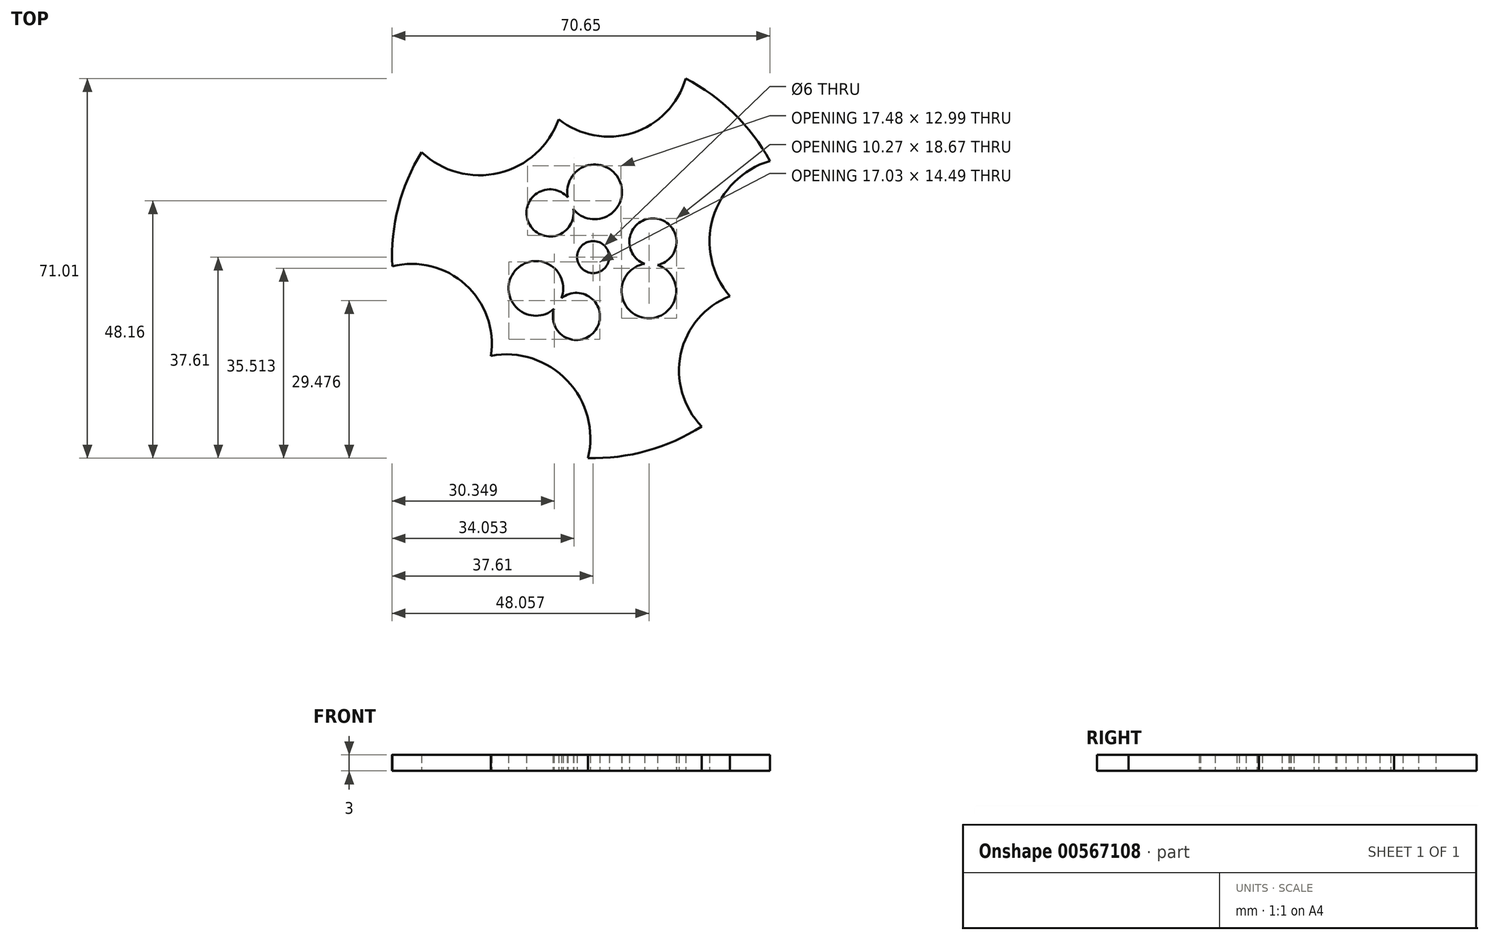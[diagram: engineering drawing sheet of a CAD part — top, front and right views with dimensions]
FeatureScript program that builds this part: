
annotation { "Feature Type Name" : "Feature", "Feature Type Description" : "" }
export const myFeature = defineFeature(function(context is Context, id is Id, definition is map)
    precondition{}
    {
        {
            var Q0;
            Q0=qCreatedBy(makeId("Top.planeOp"),FACE);
            var sketch = newSketch(context, id + "F0", { "sketchPlane" : qUnion([Q0])});
            skLineSegment(sketch, "E0.bottom", {"start": v(0, 75) * mm, "end": v(75, 75) * mm, "construction": true});
            skLineSegment(sketch, "E0.top", {"start": v(0, 0) * mm, "end": v(75, 0) * mm, "construction": true});
            skLineSegment(sketch, "E0.left", {"start": v(0, 75) * mm, "end": v(0, 0) * mm, "construction": true});
            skLineSegment(sketch, "E0.right", {"start": v(75, 75) * mm, "end": v(75, 0) * mm, "construction": true});
            skLineSegment(sketch, "E1", {"start": v(0, 75) * mm, "end": v(75, 0) * mm, "construction": true});
            skCircle(sketch, "E2", {"center": v(37.5, 37.5) * mm, "radius": 3 * mm});
            skCircle(sketch, "E3", {"center": v(37.5, 37.5) * mm, "radius": 37.61 * mm});
            skCircle(sketch, "E4", {"center": v(40.4, 75) * mm, "radius": 14.97 * mm});
            skCircle(sketch, "E5", {"center": v(37.77, 49.7) * mm, "radius": 5.12 * mm});
            skCircle(sketch, "E6", {"center": v(75, 40.4) * mm, "radius": 15.73 * mm});
            skCircle(sketch, "E7", {"center": v(48.68, 40.34) * mm, "radius": 4.4 * mm});
            skCircle(sketch, "E8.1.0", {"center": v(3.58, 21.26) * mm, "radius": 14.97 * mm});
            skCircle(sketch, "E8.1.1", {"center": v(16.24, 68.53) * mm, "radius": 15.73 * mm});
            skCircle(sketch, "E8.1.2", {"center": v(29.45, 45.76) * mm, "radius": 4.4 * mm});
            skCircle(sketch, "E8.1.3", {"center": v(26.8, 31.64) * mm, "radius": 5.12 * mm});
            skCircle(sketch, "E8.2.0", {"center": v(68.53, 16.24) * mm, "radius": 14.97 * mm});
            skCircle(sketch, "E8.2.1", {"center": v(21.26, 3.58) * mm, "radius": 15.73 * mm});
            skCircle(sketch, "E8.2.2", {"center": v(34.37, 26.4) * mm, "radius": 4.4 * mm});
            skCircle(sketch, "E8.2.3", {"center": v(47.92, 31.17) * mm, "radius": 5.12 * mm});
            skSolve(sketch);
        }
        {
            var Q0;
            Q0=makeQuery(id+"F0.imprint","IMPRINT",FACE,{"disambiguationData":[TD([[makeQuery(id+"F0.imprint","IMPRINT",EDGE,{"derivedFrom":sQuery(id+"F0.wireOp",EDGE,"E2")}),-1.0]])]});
            extrude(context, id + "F1", {"entities" : qUnion([Q0]), "depth" : 3 * mm, "offsetDistance" : 25 * mm});
        }
    });
